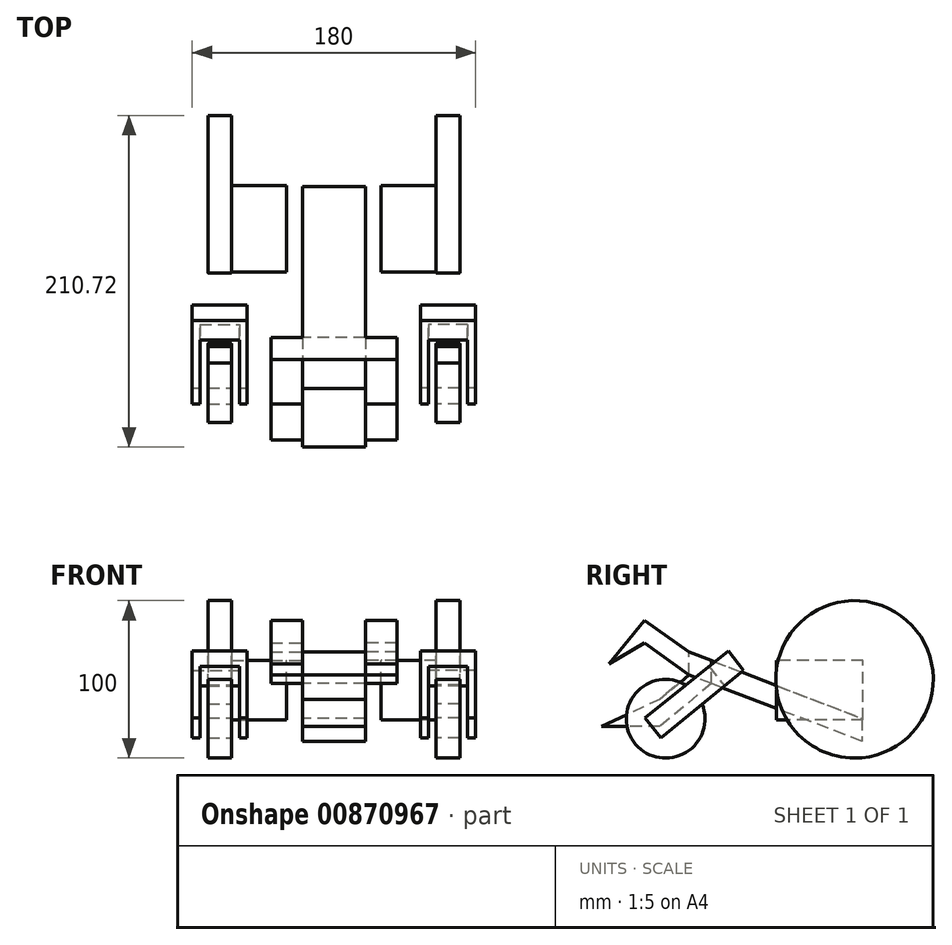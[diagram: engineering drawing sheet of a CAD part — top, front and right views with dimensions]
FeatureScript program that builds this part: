
annotation { "Feature Type Name" : "Feature", "Feature Type Description" : "" }
export const myFeature = defineFeature(function(context is Context, id is Id, definition is map)
    precondition{}
    {
        {
            var Q0;
            Q0=qCreatedBy(makeId("Right.planeOp"),FACE);
            var sketch = newSketch(context, id + "F0", { "sketchPlane" : qUnion([Q0])});
            skCircle(sketch, "E0", {"center": v(-60, 25) * mm, "radius": 25 * mm});
            skCircle(sketch, "E1", {"center": v(60, 50) * mm, "radius": 50 * mm});
            skSolve(sketch);
        }
        {
            var Q0;
            Q0=makeQuery(id+"F0.imprint","IMPRINT",FACE,{"disambiguationData":[TD([[makeQuery(id+"F0.imprint","IMPRINT",EDGE,{"derivedFrom":sQuery(id+"F0.wireOp",EDGE,"E1")}),1.0]])]});
            var Q1;
            Q1=makeQuery(id+"F0.imprint","IMPRINT",FACE,{"disambiguationData":[TD([[makeQuery(id+"F0.imprint","IMPRINT",EDGE,{"derivedFrom":sQuery(id+"F0.wireOp",EDGE,"E0")}),1.0]])]});
            extrude(context, id + "F1", {"entities" : qUnion([Q0, Q1]), "depth" : 80 * mm, "offsetDistance" : 25 * mm, "hasSecondDirection" : true, "secondDirectionOppositeDirection" : false, "secondDirectionDepth" : 65 * mm});
        }
        {
            var Q0;
            Q0=qCreatedBy(makeId("Right.planeOp"),FACE);
            var sketch = newSketch(context, id + "F2", { "sketchPlane" : qUnion([Q0])});
            skLineSegment(sketch, "E2.bottom", {"start": v(65.38, 24.34) * mm, "end": v(10.45, 24.34) * mm});
            skLineSegment(sketch, "E2.top", {"start": v(65.38, 61.91) * mm, "end": v(10.45, 61.91) * mm});
            skLineSegment(sketch, "E2.left", {"start": v(65.38, 24.34) * mm, "end": v(65.38, 61.91) * mm});
            skLineSegment(sketch, "E2.right", {"start": v(10.45, 24.34) * mm, "end": v(10.45, 61.91) * mm});
            skLineSegment(sketch, "E3", {"start": v(-63.12, 12.97) * mm, "end": v(-73.22, 25.6) * mm});
            skLineSegment(sketch, "E4", {"start": v(-73.22, 25.6) * mm, "end": v(-20.24, 67.99) * mm});
            skLineSegment(sketch, "E5", {"start": v(-20.24, 67.99) * mm, "end": v(-10.47, 55.78) * mm});
            skLineSegment(sketch, "E6", {"start": v(-10.47, 55.78) * mm, "end": v(-63.12, 12.97) * mm});
            skLineSegment(sketch, "E7", {"start": v(-32.52, 58.16) * mm, "end": v(-22.68, 45.86) * mm});
            skSolve(sketch);
        }
        {
            var Q0;
            {var subQ0=sQuery(id+"F2.wireOp",EDGE,"E5");Q0=makeQuery(id+"F2.imprint","IMPRINT",FACE,{"disambiguationData":[TD([[makeQuery(id+"F2.imprint","IMPRINT",EDGE,{"derivedFrom":subQ0}),-1.0]])]});}
            var Q1;
            {var subQ0=sQuery(id+"F2.wireOp",EDGE,"E3");Q1=makeQuery(id+"F2.imprint","IMPRINT",FACE,{"disambiguationData":[TD([[makeQuery(id+"F2.imprint","IMPRINT",EDGE,{"derivedFrom":subQ0}),-1.0]])]});}
            extrude(context, id + "F3", {"entities" : qUnion([Q0, Q1]), "depth" : 90 * mm, "offsetDistance" : 25 * mm, "hasSecondDirection" : true, "secondDirectionOppositeDirection" : false, "secondDirectionDepth" : 55 * mm});
        }
        {
            var Q0;
            Q0=makeQuery(id+"F2.imprint","IMPRINT",FACE,{"disambiguationData":[TD([[makeQuery(id+"F2.imprint","IMPRINT",EDGE,{"derivedFrom":sQuery(id+"F2.wireOp",EDGE,"E2.bottom")}),-1.0]])]});
            var Q1;
            Q1=makeQuery(id+"F1.opExtrude","CAP_FACE",FACE,{"disambiguationData":[OSD([sQuery(id+"F0.wireOp",EDGE,"E1")])],"isStart":true});
            extrude(context, id + "F4", {"entities" : qUnion([Q0]), "endBound" : BoundingType.UP_TO_SURFACE, "depth" : 25 * mm, "endBoundEntityFace" : qUnion([Q1]), "offsetDistance" : 25 * mm, "hasSecondDirection" : true, "secondDirectionOppositeDirection" : false, "secondDirectionDepth" : 30 * mm});
        }
        {
            var Q0;
            {var subQ0=sQuery(id+"F2.wireOp",EDGE,"E3");Q0=makeQuery(id+"F2.imprint","IMPRINT",FACE,{"disambiguationData":[TD([[makeQuery(id+"F2.imprint","IMPRINT",EDGE,{"derivedFrom":subQ0}),-1.0]])]});}
            extrude(context, id + "F5", {"entities" : qUnion([Q0]), "operationType" : NewBodyOperationType.REMOVE, "depth" : 85 * mm, "offsetDistance" : 25 * mm, "hasSecondDirection" : true, "secondDirectionOppositeDirection" : false, "secondDirectionDepth" : 60 * mm});
        }
        {
            var Q0;
            Q0=qCreatedBy(makeId("Right.planeOp"),FACE);
            var sketch = newSketch(context, id + "F6", { "sketchPlane" : qUnion([Q0])});
            skLineSegment(sketch, "E8", {"start": v(64.78, 10.63) * mm, "end": v(-45.08, 52.8) * mm});
            skLineSegment(sketch, "E9", {"start": v(-45.08, 52.8) * mm, "end": v(-45.08, 67.33) * mm});
            skLineSegment(sketch, "E10", {"start": v(-45.08, 67.33) * mm, "end": v(64.78, 25.16) * mm});
            skLineSegment(sketch, "E11", {"start": v(64.78, 25.16) * mm, "end": v(64.78, 10.63) * mm});
            skLineSegment(sketch, "E12", {"start": v(-30.95, 47.37) * mm, "end": v(-63.5, 20.2) * mm});
            skLineSegment(sketch, "E13", {"start": v(-63.5, 20.2) * mm, "end": v(-100.72, 20.2) * mm});
            skLineSegment(sketch, "E14", {"start": v(-45.08, 52.8) * mm, "end": v(-63.5, 37.42) * mm});
            skLineSegment(sketch, "E15", {"start": v(-63.5, 37.42) * mm, "end": v(-100.72, 20.2) * mm});
            skLineSegment(sketch, "E16", {"start": v(-45.08, 52.8) * mm, "end": v(-73.43, 73) * mm});
            skLineSegment(sketch, "E17", {"start": v(-73.43, 73) * mm, "end": v(-96.11, 59.89) * mm});
            skLineSegment(sketch, "E18", {"start": v(-45.08, 67.33) * mm, "end": v(-73.43, 87.53) * mm});
            skLineSegment(sketch, "E19", {"start": v(-73.43, 87.53) * mm, "end": v(-96.11, 59.89) * mm});
            skLineSegment(sketch, "E20", {"start": v(-30.95, 47.37) * mm, "end": v(-30.95, 61.9) * mm});
            skSolve(sketch);
        }
        {
            var Q0;
            {var subQ0=sQuery(id+"F6.wireOp",EDGE,"E11");Q0=makeQuery(id+"F6.imprint","IMPRINT",FACE,{"disambiguationData":[TD([[makeQuery(id+"F6.imprint","IMPRINT",EDGE,{"derivedFrom":subQ0}),-1.0]])]});}
            var Q1;
            {var subQ0=sQuery(id+"F6.wireOp",EDGE,"E9");Q1=makeQuery(id+"F6.imprint","IMPRINT",FACE,{"disambiguationData":[TD([[makeQuery(id+"F6.imprint","IMPRINT",EDGE,{"derivedFrom":subQ0}),-1.0]])]});}
            var Q2;
            {var subQ1=sQuery(id+"F6.wireOp",EDGE,"E12");Q2=makeQuery(id+"F6.imprint","IMPRINT",FACE,{"disambiguationData":[TD([[makeQuery(id+"F6.imprint","IMPRINT",EDGE,{"derivedFrom":subQ1}),-1.0]])]});}
            extrude(context, id + "F7", {"entities" : qUnion([Q0, Q1, Q2]), "endBound" : BoundingType.SYMMETRIC, "depth" : 40 * mm, "offsetDistance" : 25 * mm});
        }
        {
            var Q0;
            {var subQ0=sQuery(id+"F6.wireOp",EDGE,"E9");Q0=makeQuery(id+"F6.imprint","IMPRINT",FACE,{"disambiguationData":[TD([[makeQuery(id+"F6.imprint","IMPRINT",EDGE,{"derivedFrom":subQ0}),-1.0]])]});}
            var Q1;
            Q1=makeQuery(id+"F6.imprint","IMPRINT",FACE,{"disambiguationData":[TD([[makeQuery(id+"F6.imprint","IMPRINT",EDGE,{"derivedFrom":sQuery(id+"F6.wireOp",EDGE,"E9")}),1.0]])]});
            var Q2;
            Q2=makeQuery(id+"F7.opExtrude","CAP_FACE",FACE,{"disambiguationData":[OSD([sQuery(id+"F6.wireOp",EDGE,"E8"),sQuery(id+"F6.wireOp",EDGE,"E9"),sQuery(id+"F6.wireOp",EDGE,"E10"),sQuery(id+"F6.wireOp",EDGE,"E11"),sQuery(id+"F6.wireOp",EDGE,"E12"),sQuery(id+"F6.wireOp",EDGE,"E13"),sQuery(id+"F6.wireOp",EDGE,"E14"),sQuery(id+"F6.wireOp",EDGE,"E15")])],"isStart":false});
            extrude(context, id + "F8", {"entities" : qUnion([Q0, Q1]), "depth" : 40 * mm, "offsetDistance" : 25 * mm, "hasSecondDirection" : true, "secondDirectionBound" : SecondDirectionBoundingType.UP_TO_SURFACE, "secondDirectionOppositeDirection" : false, "secondDirectionDepth" : 25 * mm, "secondDirectionBoundEntityFace" : qUnion([Q2])});
        }
        {
            var Q0;
            Q0=makeQuery(id+"F8.opExtrude","SWEPT_BODY",BODY,{"disambiguationData":[OSD([sQuery(id+"F6.wireOp",EDGE,"E8"),sQuery(id+"F6.wireOp",EDGE,"E10"),sQuery(id+"F6.wireOp",EDGE,"E16"),sQuery(id+"F6.wireOp",EDGE,"E17"),sQuery(id+"F6.wireOp",EDGE,"E18"),sQuery(id+"F6.wireOp",EDGE,"E19"),sQuery(id+"F6.wireOp",EDGE,"E20")])]});
            var Q1;
            Q1=makeQuery(id+"F1.opExtrude","SWEPT_BODY",BODY,{"disambiguationData":[OSD([sQuery(id+"F0.wireOp",EDGE,"E0")])]});
            var Q2;
            Q2=makeQuery(id+"F3.opExtrude","SWEPT_BODY",BODY,{"disambiguationData":[OSD([sQuery(id+"F2.wireOp",EDGE,"E3"),sQuery(id+"F2.wireOp",EDGE,"E4"),sQuery(id+"F2.wireOp",EDGE,"E5"),sQuery(id+"F2.wireOp",EDGE,"E6")])]});
            var Q3;
            Q3=makeQuery(id+"F4.opExtrude","SWEPT_BODY",BODY,{"disambiguationData":[OSD([sQuery(id+"F2.wireOp",EDGE,"E2.bottom"),sQuery(id+"F2.wireOp",EDGE,"E2.top"),sQuery(id+"F2.wireOp",EDGE,"E2.left"),sQuery(id+"F2.wireOp",EDGE,"E2.right")])]});
            var Q4;
            Q4=makeQuery(id+"F1.opExtrude","SWEPT_BODY",BODY,{"disambiguationData":[OSD([sQuery(id+"F0.wireOp",EDGE,"E1")])]});
            var Q5;
            Q5=qCreatedBy(makeId("Right.planeOp"),FACE);
            mirror(context, id + "F9", {"operationType" : NewBodyOperationType.ADD, "entities" : qUnion([Q0, Q1, Q2, Q3, Q4]), "mirrorPlane" : qUnion([Q5])});
        }
    });
